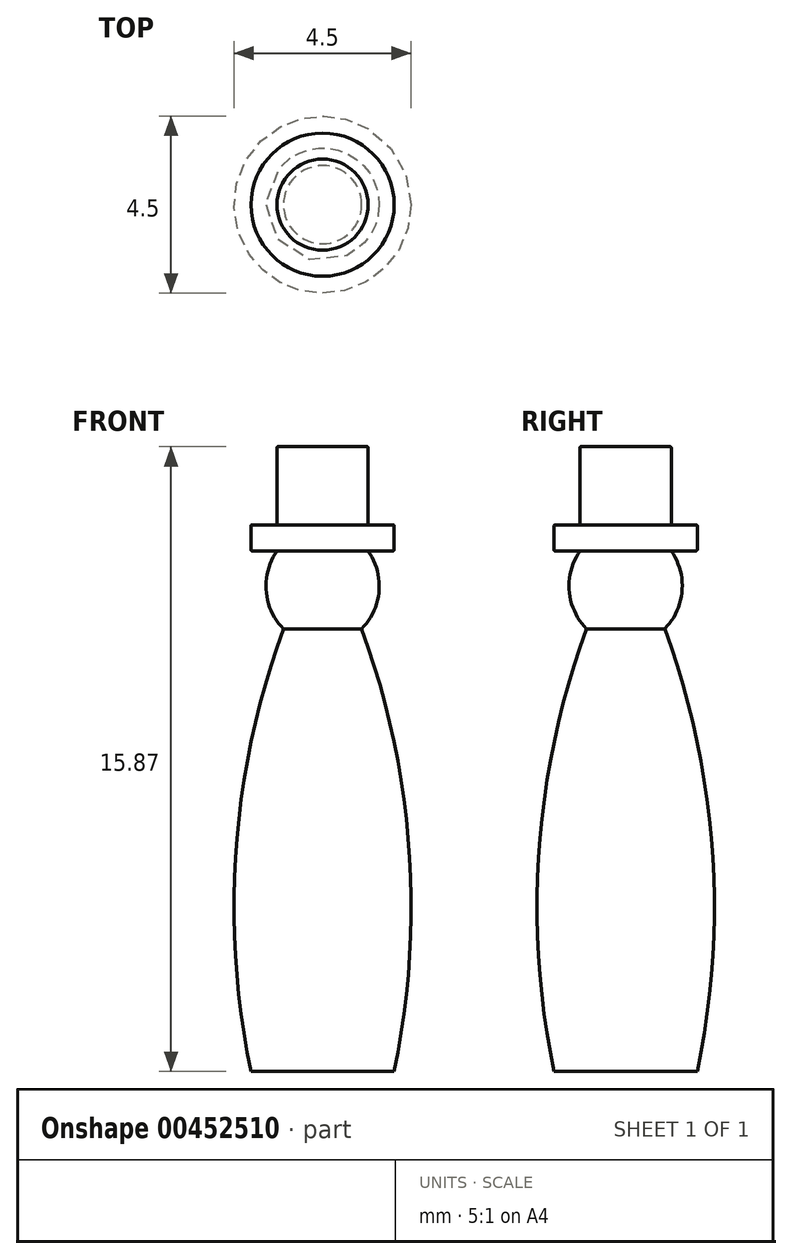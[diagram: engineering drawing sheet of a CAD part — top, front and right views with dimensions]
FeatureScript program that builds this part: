
annotation { "Feature Type Name" : "Feature", "Feature Type Description" : "" }
export const myFeature = defineFeature(function(context is Context, id is Id, definition is map)
    precondition{}
    {
        {
            var Q0;
            Q0=qCreatedBy(makeId("Front.planeOp"),FACE);
            var sketch = newSketch(context, id + "F0", { "sketchPlane" : qUnion([Q0])});
            skLineSegment(sketch, "E0", {"start": v(0, 8.14) * mm, "end": v(0, -7.73) * mm});
            skLineSegment(sketch, "E1.bottom", {"start": v(0, 8.14) * mm, "end": v(1.16, 8.14) * mm});
            skLineSegment(sketch, "E1.top", {"start": v(0, 6.16) * mm, "end": v(1.16, 6.16) * mm});
            skLineSegment(sketch, "E1.left", {"start": v(0, 8.14) * mm, "end": v(0, 6.16) * mm});
            skLineSegment(sketch, "E1.right", {"start": v(1.16, 8.14) * mm, "end": v(1.16, 6.16) * mm});
            skLineSegment(sketch, "E2.bottom", {"start": v(0, 6.16) * mm, "end": v(1.82, 6.16) * mm});
            skLineSegment(sketch, "E2.top", {"start": v(0, 5.5) * mm, "end": v(1.82, 5.5) * mm});
            skLineSegment(sketch, "E2.left", {"start": v(0, 6.16) * mm, "end": v(0, 5.5) * mm});
            skLineSegment(sketch, "E2.right", {"start": v(1.82, 6.16) * mm, "end": v(1.82, 5.5) * mm});
            skLineSegment(sketch, "E3.bottom", {"start": v(0, 3.51) * mm, "end": v(1, 3.51) * mm});
            skLineSegment(sketch, "E3.top", {"start": v(0, -7.73) * mm, "end": v(1, -7.73) * mm});
            skLineSegment(sketch, "E3.left", {"start": v(0, 3.51) * mm, "end": v(0, -7.73) * mm});
            skArc(sketch, "E4", {"start": v(1, 3.51) * mm, "mid": v(1.43, 4.47) * mm, "end": v(1.16, 5.5) * mm});
            skPoint(sketch, "E4.second.point", {"position": v(1.16, 5.5) * mm});
            skLineSegment(sketch, "E5", {"start": v(0, -7.73) * mm, "end": v(1.82, -7.73) * mm});
            skArc(sketch, "E6", {"start": v(1.82, -7.73) * mm, "mid": v(2.2, -2.05) * mm, "end": v(1, 3.51) * mm});
            skSolve(sketch);
        }
        {
            var Q0;
            Q0 = qSketchRegion(id + "F0", true);
            var Q1;
            Q1=sQuery(id+"F0.wireOp",EDGE,"E0");
            revolve(context, id + "F1", {"entities" : qUnion([Q0]), "axis" : qUnion([Q1]), "revolveType" : RevolveType.FULL});
        }
        {
            var Q0;
            Q0=makeQuery(id+"F1.opRevolve","SWEPT_EDGE",EDGE,{"disambiguationData":[OSD([sQuery(id+"F0.wireOp",EDGE,"E1.bottom"),sQuery(id+"F0.wireOp",EDGE,"E1.right")])]});
            var Q1;
            Q1=makeQuery(id+"F1.opRevolve","SWEPT_EDGE",EDGE,{"disambiguationData":[OSD([sQuery(id+"F0.wireOp",EDGE,"E2.bottom"),sQuery(id+"F0.wireOp",EDGE,"E2.right")])]});
            var Q2;
            Q2=makeQuery(id+"F1.opRevolve","SWEPT_EDGE",EDGE,{"disambiguationData":[OSD([sQuery(id+"F0.wireOp",EDGE,"E2.top"),sQuery(id+"F0.wireOp",EDGE,"E2.right")])]});
            var Q3;
            Q3=makeQuery(id+"F1.opRevolve","SWEPT_EDGE",EDGE,{"disambiguationData":[OSD([sQuery(id+"F0.wireOp",EDGE,"E1.right"),sQuery(id+"F0.wireOp",EDGE,"E2.bottom")])]});
            fillet(context, id + "F2", {"entities" : qUnion([Q0, Q1, Q2, Q3]), "radius" : 0.03 * mm, "tangentPropagation" : true, "allowEdgeOverflow" : false});
        }
    });
